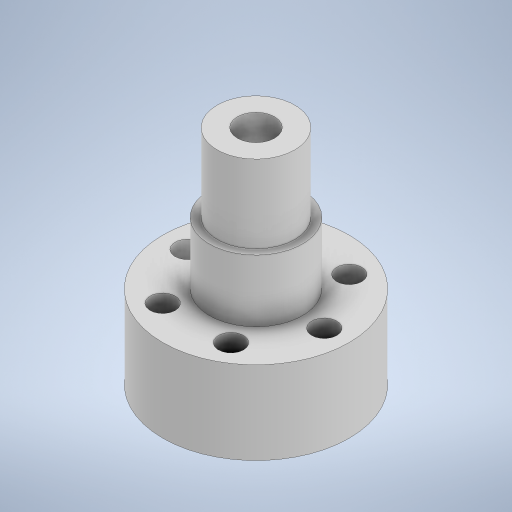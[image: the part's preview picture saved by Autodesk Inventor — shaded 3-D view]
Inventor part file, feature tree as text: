
AUTODESK INVENTOR PART (.ipt)
format: ipt  version: 2024 (Build 280153000, 153)  size: 283,136 bytes
history: native  units: mm
features: extrude x5, sketch x5, projected_geometry x1
ambient origin geometry x8: Origin, YZ Plane, XZ Plane, XY Plane, X Axis, Y Axis, Z Axis, Center Point
bodies: Solid1 (feature_tree)
feature tree (11):
  extrude  "Extrusion1"  Depth=20.0mm TaperAngle=0.0deg
  extrude  "Extrusion2"  Depth=25.0mm TaperAngle=0.0deg
  extrude  "Extrusion3"  Depth=60.0mm
  extrude  "Extrusion4"  Depth=10.0mm
  extrude  "Extrusion5"  Depth=22.0mm
  sketch  "Sketch1"  dims[d0=30.0mm d1=20.0mm d2=0.0mm]
  sketch  "Sketch2"  dims[d3=25.0mm d4=25.0mm d5=0.0mm]
  sketch  "Sketch3"  dims[d6=100.0mm d7=0.0mm d8=60.0mm]
  sketch  "Sketch4"  dims[d9=10.0mm d10=0.0mm d11=12.0mm]
  sketch  "Sketch5"  dims[d12=22.0mm d13=8.1mm d14=60.0mm d16=360.0deg d18=16.7mm d19=0.0mm]
  projected_geometry  "Projected Loop1"
